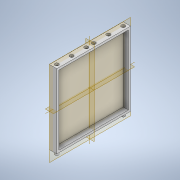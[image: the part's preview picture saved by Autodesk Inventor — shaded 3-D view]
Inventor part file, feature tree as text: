
AUTODESK INVENTOR PART (.ipt)
format: ipt  version: 2022.4 (Build 264492010, 492A)  size: 158,720 bytes
history: native  units: mm
features: extrude x4, sketch x4
ambient origin geometry x8: Origin, YZ Plane, XZ Plane, XY Plane, X Axis, Y Axis, Z Axis, Center Point
bodies: Solid1 (feature_tree)
feature tree (8):
  extrude  "Extrusion1"  Depth=100.0mm
  extrude  "Extrusion2"  Depth=94.0mm
  extrude  "Extrusion3"  Depth=7.0mm TaperAngle=0.0deg
  extrude  "Extrusion4"  Depth=5.0mm
  sketch  "Sketch2"  dims[d0=100.0mm d1=100.0mm]
  sketch  "Sketch3"  dims[d2=10.0mm d3=0.0mm d4=94.0mm]
  sketch  "Sketch5"  dims[d5=94.0mm d6=7.0mm d7=0.0mm]
  sketch  "Sketch6"  dims[d26=5.0mm d27=5.0mm d28=30.0mm d30=20.0mm d31=10.0mm d33=10.0mm d35=5.0mm d36=5.0mm d37=30.0mm d39=20.0mm d40=10.0mm d42=10.0mm d44=7.0mm d45=0.0mm d46=5.0mm d47=5.0mm d64=5.0mm d65=0.0mm]
